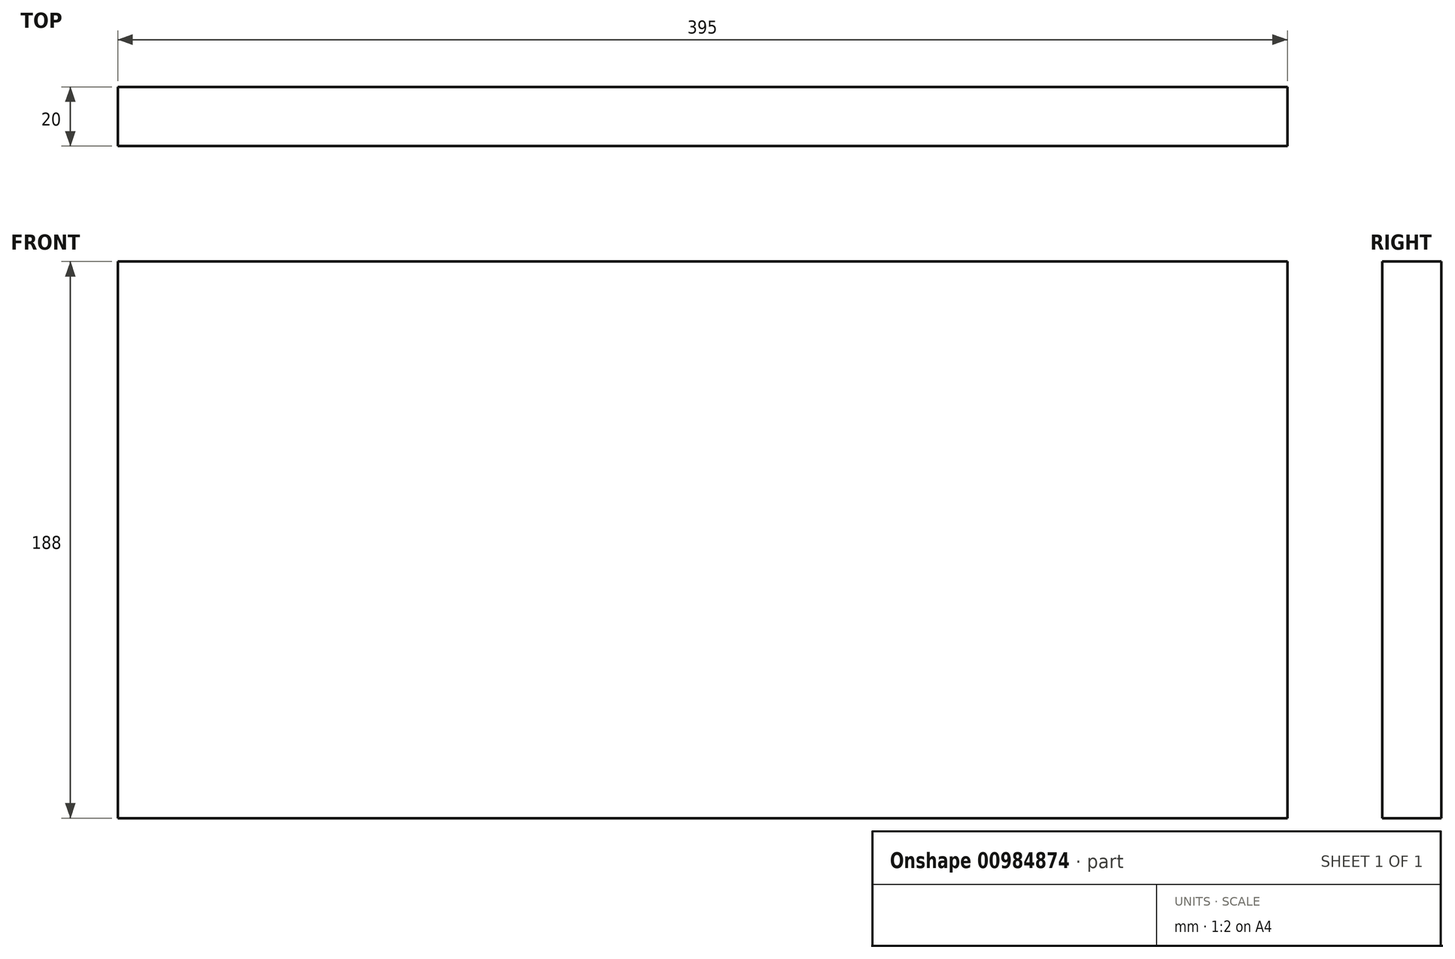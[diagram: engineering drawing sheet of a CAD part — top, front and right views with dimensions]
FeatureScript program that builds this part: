
annotation { "Feature Type Name" : "Feature", "Feature Type Description" : "" }
export const myFeature = defineFeature(function(context is Context, id is Id, definition is map)
    precondition{}
    {
        {
            var Q0;
            Q0=qCreatedBy(makeId("Front.planeOp"),FACE);
            var sketch = newSketch(context, id + "F0", { "sketchPlane" : qUnion([Q0])});
            skLineSegment(sketch, "E0.bottom", {"start": v(0, 0) * mm, "end": v(395, 0) * mm});
            skLineSegment(sketch, "E0.top", {"start": v(0, 188) * mm, "end": v(395, 188) * mm});
            skLineSegment(sketch, "E0.left", {"start": v(0, 0) * mm, "end": v(0, 188) * mm});
            skLineSegment(sketch, "E0.right", {"start": v(395, 0) * mm, "end": v(395, 188) * mm});
            skSolve(sketch);
        }
        {
            var Q0;
            Q0=makeQuery(id+"F0.imprint","IMPRINT",FACE,{"disambiguationData":[TD([[makeQuery(id+"F0.imprint","IMPRINT",EDGE,{"derivedFrom":sQuery(id+"F0.wireOp",EDGE,"E0.bottom")}),1.0]])]});
            extrude(context, id + "F1", {"entities" : qUnion([Q0]), "oppositeDirection" : true, "depth" : 20 * mm, "offsetDistance" : 25 * mm});
        }
    });
